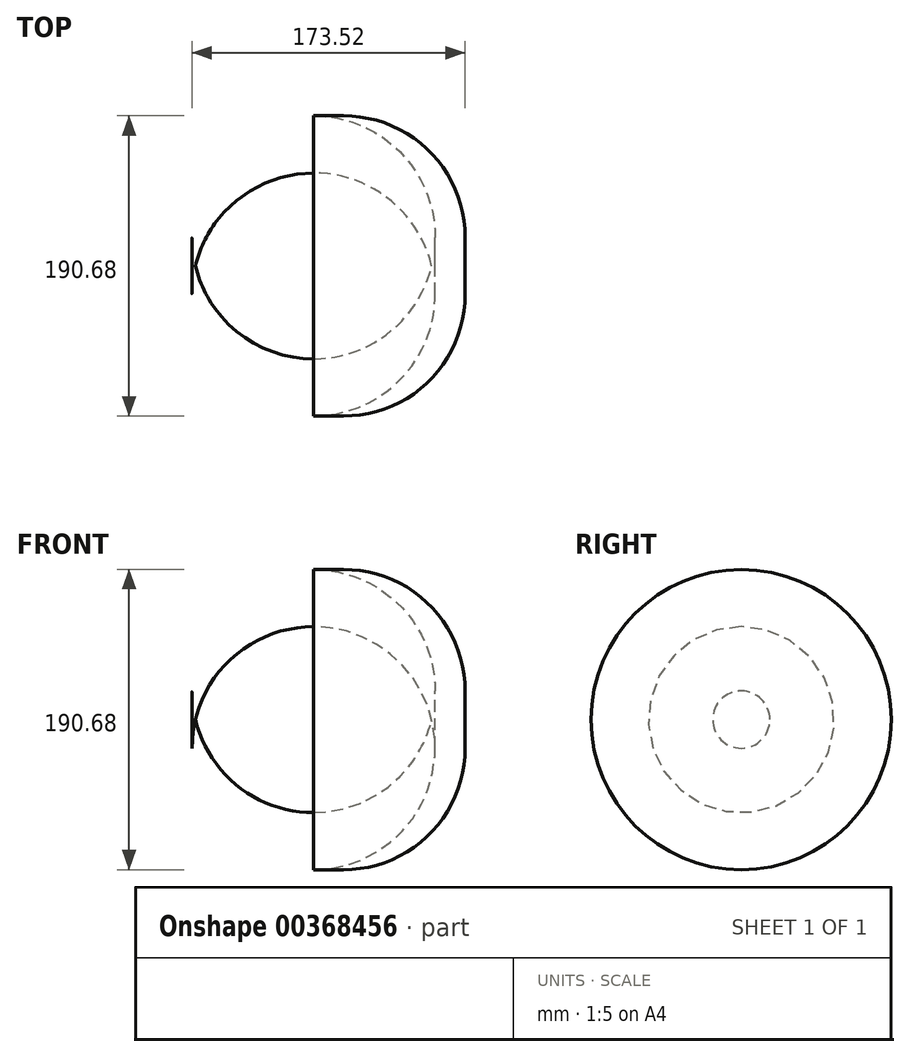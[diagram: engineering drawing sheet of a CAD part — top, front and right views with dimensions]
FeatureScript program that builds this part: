
annotation { "Feature Type Name" : "Feature", "Feature Type Description" : "" }
export const myFeature = defineFeature(function(context is Context, id is Id, definition is map)
    precondition{}
    {
        {
            var Q0;
            Q0=qCreatedBy(makeId("Right.planeOp"),FACE);
            var sketch = newSketch(context, id + "F0", { "sketchPlane" : qUnion([Q0])});
            skCircle(sketch, "E0", {"center": v(0, 0.24) * mm, "radius": 95.34 * mm});
            skSolve(sketch);
        }
        {
            var Q0;
            Q0 = qSketchRegion(id + "F0", true);
            extrude(context, id + "F1", {"entities" : qUnion([Q0]), "endBound" : BoundingType.SYMMETRIC, "depth" : 173.52 * mm});
        }
        {
            var Q0;
            Q0=makeQuery(id+"F1.opExtrude","CAP_FACE",FACE,{"disambiguationData":[OSD([sQuery(id+"F0.wireOp",EDGE,"E0")])],"isStart":true});
            var Q1;
            Q1=makeQuery(id+"F1.opExtrude","CAP_FACE",FACE,{"disambiguationData":[OSD([sQuery(id+"F0.wireOp",EDGE,"E0")])],"isStart":false});
            fillet(context, id + "F2", {"entities" : qUnion([Q0, Q1]), "radius" : 77.19 * mm, "tangentPropagation" : true, "allowEdgeOverflow" : false});
        }
        {
            var Q0;
            Q0=qCreatedBy(makeId("Top.planeOp"),FACE);
            var sketch = newSketch(context, id + "F3", { "sketchPlane" : qUnion([Q0])});
            skFitSpline(sketch, "E1", {"points": [v(-86.72, 0) * mm, v(-117.93, 0) * mm, v(-135, -16.99) * mm, v(-168.63, 0) * mm, v(-238.36, 28.19) * mm, v(-290.8, -22.13) * mm, v(-299.01, -39.52) * mm, v(-303.78, -43.7) * mm], "startDerivative": vector(-255.62, 54.78) * mm, "endDerivative": vector(-82.53, -55.78) * mm});
            skSolve(sketch);
        }
        {
            var Q0;
            Q0 = qSketchRegion(id + "F3", true);
            var Q1;
            Q1=sQuery(id+"F3.wireOp",EDGE,"E1");
            extrude(context, id + "F4", {"entities" : qUnion([Q0]), "bodyType" : ToolBodyType.SURFACE, "operationType" : NewBodyOperationType.ADD, "surfaceEntities" : qUnion([Q1]), "endBound" : BoundingType.SYMMETRIC, "depth" : 17.01 * mm});
        }
    });
